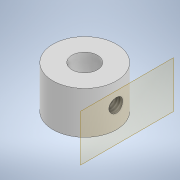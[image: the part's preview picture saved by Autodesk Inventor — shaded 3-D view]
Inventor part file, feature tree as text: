
AUTODESK INVENTOR PART (.ipt)
format: ipt  version: 2021.3 (Build 253353000, 353)  size: 112,128 bytes
history: native  units: mm
features: sketch x2, extrude x1, plane x1, hole x1
ambient origin geometry x8: Origin, YZ Plane, XZ Plane, XY Plane, X Axis, Y Axis, Z Axis, Center Point
bodies: Volumenkörper1 (feature_tree)
feature tree (5):
  extrude  "Extrusion1"  Depth=15.0mm
  plane  "Arbeitsebene1"
  hole  "Bohrung1"  [1 undecoded]
  sketch  "Skizze1"  dims[d0=6.0mm d1=15.0mm]
  sketch  "Skizze3"  dims[d2=10.0mm d3=0.0mm d4=10.0mm d5=3.242mm d6=8.0mm d7=4.0mm d8=2.0mm d9=90.0deg d10=11.8mm d11=20.594885mm]
note: 1 required parameter value undecoded (feature->parameter linkage not recoverable at this tier; creation-order binding heuristic only, values carry confidence <= 0.55)
